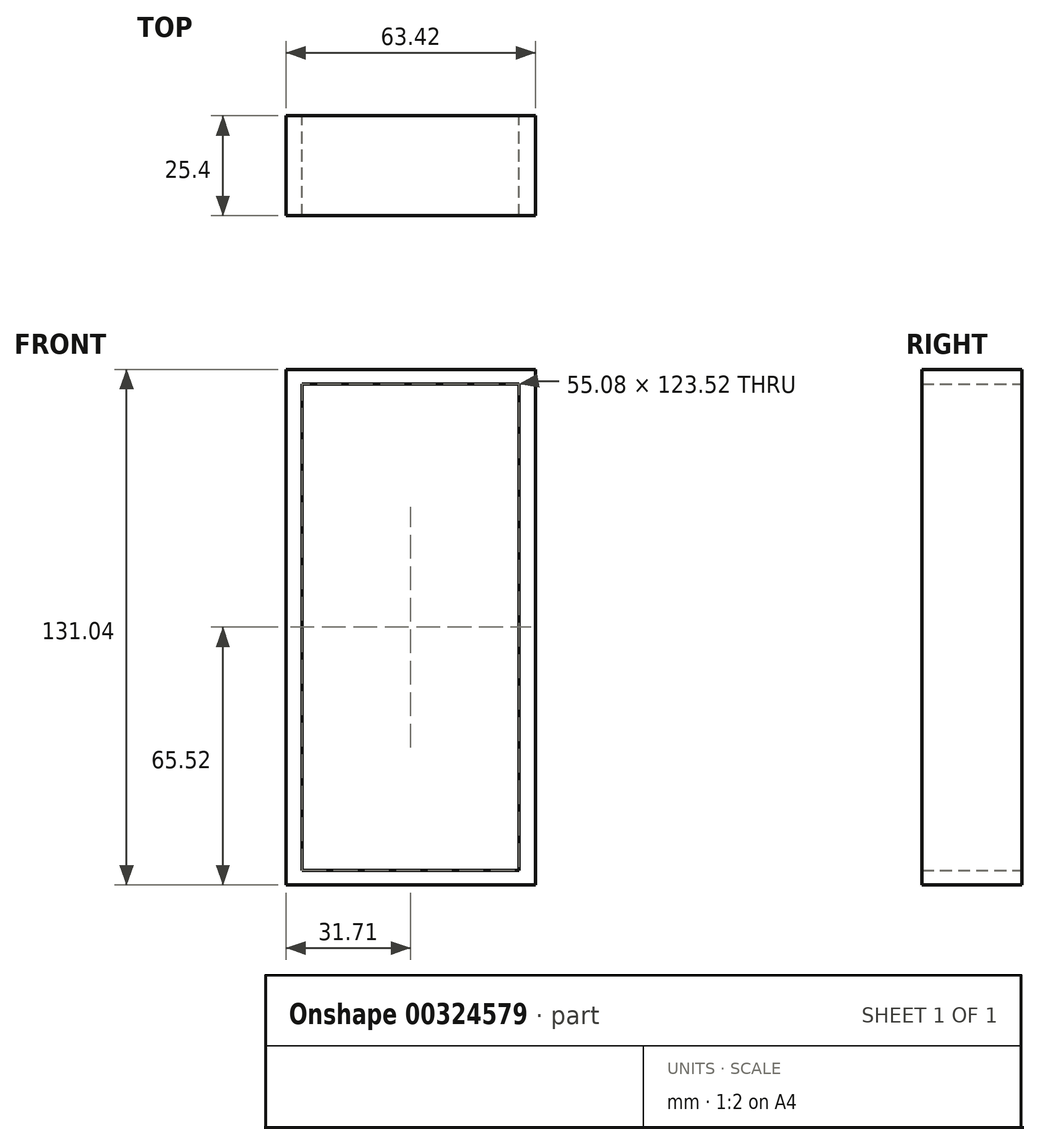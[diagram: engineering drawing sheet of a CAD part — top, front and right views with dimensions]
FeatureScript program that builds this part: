
annotation { "Feature Type Name" : "Feature", "Feature Type Description" : "" }
export const myFeature = defineFeature(function(context is Context, id is Id, definition is map)
    precondition{}
    {
        {
            var Q0;
            Q0=qCreatedBy(makeId("Front.planeOp"),FACE);
            var sketch = newSketch(context, id + "F0", { "sketchPlane" : qUnion([Q0])});
            skLineSegment(sketch, "E0.bottom", {"start": v(-31.71, 65.52) * mm, "end": v(31.71, 65.52) * mm});
            skLineSegment(sketch, "E0.top", {"start": v(-31.71, -65.52) * mm, "end": v(31.71, -65.52) * mm});
            skLineSegment(sketch, "E0.left", {"start": v(-31.71, 65.52) * mm, "end": v(-31.71, -65.52) * mm});
            skLineSegment(sketch, "E0.right", {"start": v(31.71, 65.52) * mm, "end": v(31.71, -65.52) * mm});
            skPoint(sketch, "E0.middle", {"position": v(0, 0) * mm});
            skLineSegment(sketch, "E1.bottom", {"start": v(-27.54, 61.76) * mm, "end": v(27.54, 61.76) * mm});
            skLineSegment(sketch, "E1.top", {"start": v(-27.54, -61.76) * mm, "end": v(27.54, -61.76) * mm});
            skLineSegment(sketch, "E1.left", {"start": v(-27.54, 61.76) * mm, "end": v(-27.54, -61.76) * mm});
            skLineSegment(sketch, "E1.right", {"start": v(27.54, 61.76) * mm, "end": v(27.54, -61.76) * mm});
            skLineSegment(sketch, "E2", {"start": v(-27.54, 4.6) * mm, "end": v(27.54, 4.6) * mm});
            skLineSegment(sketch, "E3", {"start": v(-27.54, 0) * mm, "end": v(27.54, 0) * mm});
            skFitSpline(sketch, "E4", {"points": [v(-27.54, 61.76) * mm, v(0, 4.6) * mm, v(27.54, 61.76) * mm], "startDerivative": vector(55.08, -171.51) * mm, "endDerivative": vector(55.08, 171.51) * mm});
            skLineSegment(sketch, "E5", {"start": v(-23.26, 48.55) * mm, "end": v(-23.26, 4.6) * mm});
            skLineSegment(sketch, "E6", {"start": v(24, 50.82) * mm, "end": v(24, 4.6) * mm});
            skLineSegment(sketch, "E7", {"start": v(19.97, 38.78) * mm, "end": v(19.97, 4.6) * mm});
            skLineSegment(sketch, "E8", {"start": v(-19.39, 37.11) * mm, "end": v(-18.36, 4.6) * mm});
            skLineSegment(sketch, "E9", {"start": v(-15.52, 26.7) * mm, "end": v(-15.52, 4.6) * mm});
            skLineSegment(sketch, "E10", {"start": v(14.85, 25.04) * mm, "end": v(14.85, 4.6) * mm});
            skLineSegment(sketch, "E11", {"start": v(-9.61, 13.82) * mm, "end": v(-9.61, 4.6) * mm});
            skLineSegment(sketch, "E12", {"start": v(9.71, 14) * mm, "end": v(9.71, 4.6) * mm});
            skSolve(sketch);
        }
        {
            var Q0;
            Q0 = qSketchRegion(id + "F0", true);
            extrude(context, id + "F1", {"entities" : qUnion([Q0]), "depth" : 25.4 * mm});
        }
    });
